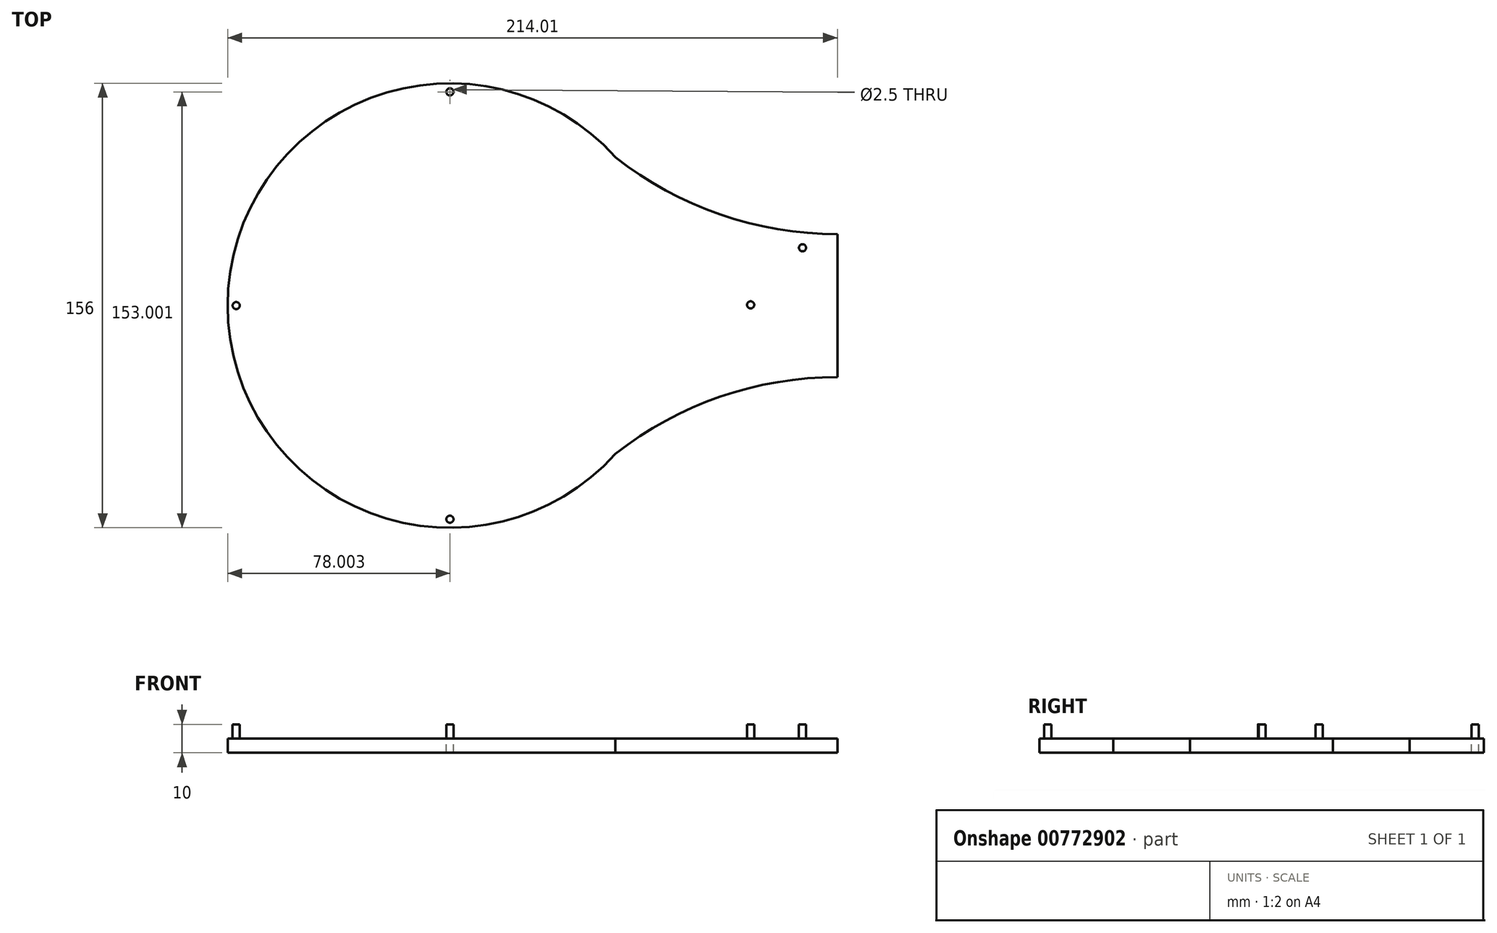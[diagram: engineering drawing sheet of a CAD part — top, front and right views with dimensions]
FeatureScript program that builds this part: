
annotation { "Feature Type Name" : "Feature", "Feature Type Description" : "" }
export const myFeature = defineFeature(function(context is Context, id is Id, definition is map)
    precondition{}
    {
        {
            var Q0;
            Q0=qCreatedBy(makeId("Top.planeOp"),FACE);
            var sketch = newSketch(context, id + "F0", { "sketchPlane" : qUnion([Q0])});
            skArc(sketch, "E0.1", {"start": v(-25.7, 50.9) * mm, "mid": v(-161.83, -1.11) * mm, "end": v(-25.7, -53.14) * mm});
            skLineSegment(sketch, "E0.3", {"start": v(52.19, 17.91) * mm, "end": v(52.17, -20.18) * mm});
            skLineSegment(sketch, "E1", {"start": v(52.18, -1.13) * mm, "end": v(52.18, 23.97) * mm});
            skLineSegment(sketch, "E2", {"start": v(52.18, 23.97) * mm, "end": v(52.18, -26.23) * mm});
            skArc(sketch, "E3", {"start": v(-25.7, 50.9) * mm, "mid": v(10.98, 30.9) * mm, "end": v(52.18, 23.97) * mm});
            skArc(sketch, "E4", {"start": v(52.18, -26.23) * mm, "mid": v(10.97, -33.14) * mm, "end": v(-25.7, -53.14) * mm});
            skPoint(sketch, "E5.startSnap0", {"position": v(-161.83, -1.11) * mm});
            skCircle(sketch, "E6", {"center": v(-83.83, 73.88) * mm, "radius": 1.25 * mm});
            skCircle(sketch, "E7", {"center": v(-158.83, -1.13) * mm, "radius": 1.25 * mm});
            skCircle(sketch, "E8", {"center": v(-83.83, -76.12) * mm, "radius": 1.25 * mm});
            skCircle(sketch, "E9", {"center": v(21.7, -0.89) * mm, "radius": 1.25 * mm});
            skCircle(sketch, "E10", {"center": v(39.93, 19.15) * mm, "radius": 1.25 * mm});
            skSolve(sketch);
        }
        {
            var Q0;
            Q0=makeQuery(id+"F0.imprint","IMPRINT",FACE,{"disambiguationData":[TD([[makeQuery(id+"F0.imprint","IMPRINT",EDGE,{"derivedFrom":sQuery(id+"F0.wireOp",EDGE,"E0.1")}),1.0]])]});
            extrude(context, id + "F1", {"entities" : qUnion([Q0]), "oppositeDirection" : true, "depth" : 5 * mm, "offsetDistance" : 25 * mm});
        }
        {
            var Q0;
            Q0=makeQuery(id+"F0.imprint","IMPRINT",FACE,{"disambiguationData":[TD([[makeQuery(id+"F0.imprint","IMPRINT",EDGE,{"derivedFrom":sQuery(id+"F0.wireOp",EDGE,"E10")}),1.0]])]});
            var Q1;
            Q1=makeQuery(id+"F0.imprint","IMPRINT",FACE,{"disambiguationData":[TD([[makeQuery(id+"F0.imprint","IMPRINT",EDGE,{"derivedFrom":sQuery(id+"F0.wireOp",EDGE,"E9")}),1.0]])]});
            var Q2;
            Q2=makeQuery(id+"F0.imprint","IMPRINT",FACE,{"disambiguationData":[TD([[makeQuery(id+"F0.imprint","IMPRINT",EDGE,{"derivedFrom":sQuery(id+"F0.wireOp",EDGE,"E6")}),1.0]])]});
            var Q3;
            Q3=makeQuery(id+"F0.imprint","IMPRINT",FACE,{"disambiguationData":[TD([[makeQuery(id+"F0.imprint","IMPRINT",EDGE,{"derivedFrom":sQuery(id+"F0.wireOp",EDGE,"E8")}),1.0]])]});
            var Q4;
            Q4=makeQuery(id+"F0.imprint","IMPRINT",FACE,{"disambiguationData":[TD([[makeQuery(id+"F0.imprint","IMPRINT",EDGE,{"derivedFrom":sQuery(id+"F0.wireOp",EDGE,"E7")}),1.0]])]});
            extrude(context, id + "F2", {"entities" : qUnion([Q0, Q1, Q2, Q3, Q4]), "depth" : 5 * mm, "offsetDistance" : 25 * mm});
        }
        {
            var Q0;
            Q0=makeQuery(id+"F0.imprint","IMPRINT",FACE,{"disambiguationData":[TD([[makeQuery(id+"F0.imprint","IMPRINT",EDGE,{"derivedFrom":sQuery(id+"F0.wireOp",EDGE,"E7")}),1.0]])]});
            var Q1;
            Q1=makeQuery(id+"F0.imprint","IMPRINT",FACE,{"disambiguationData":[TD([[makeQuery(id+"F0.imprint","IMPRINT",EDGE,{"derivedFrom":sQuery(id+"F0.wireOp",EDGE,"E8")}),1.0]])]});
            var Q2;
            Q2=makeQuery(id+"F0.imprint","IMPRINT",FACE,{"disambiguationData":[TD([[makeQuery(id+"F0.imprint","IMPRINT",EDGE,{"derivedFrom":sQuery(id+"F0.wireOp",EDGE,"E6")}),1.0]])]});
            var Q3;
            Q3=makeQuery(id+"F0.imprint","IMPRINT",FACE,{"disambiguationData":[TD([[makeQuery(id+"F0.imprint","IMPRINT",EDGE,{"derivedFrom":sQuery(id+"F0.wireOp",EDGE,"E9")}),1.0]])]});
            var Q4;
            Q4=makeQuery(id+"F0.imprint","IMPRINT",FACE,{"disambiguationData":[TD([[makeQuery(id+"F0.imprint","IMPRINT",EDGE,{"derivedFrom":sQuery(id+"F0.wireOp",EDGE,"E10")}),1.0]])]});
            extrude(context, id + "F3", {"entities" : qUnion([Q0, Q1, Q2, Q3, Q4]), "oppositeDirection" : true, "depth" : 5 * mm, "offsetDistance" : 25 * mm});
        }
        {
            var Q0;
            Q0=makeQuery(id+"F1.opExtrude","SWEPT_BODY",BODY,{"disambiguationData":[OSD([sQuery(id+"F0.wireOp",EDGE,"E0.1"),sQuery(id+"F0.wireOp",EDGE,"E2"),sQuery(id+"F0.wireOp",EDGE,"E3"),sQuery(id+"F0.wireOp",EDGE,"E4"),sQuery(id+"F0.wireOp",EDGE,"E6"),sQuery(id+"F0.wireOp",EDGE,"E7"),sQuery(id+"F0.wireOp",EDGE,"E8"),sQuery(id+"F0.wireOp",EDGE,"E9"),sQuery(id+"F0.wireOp",EDGE,"E10")])]});
            var Q1;
            Q1=makeQuery(id+"F2.opExtrude","SWEPT_BODY",BODY,{"disambiguationData":[OSD([sQuery(id+"F0.wireOp",EDGE,"E6")])]});
            var Q2;
            Q2=makeQuery(id+"F2.opExtrude","SWEPT_BODY",BODY,{"disambiguationData":[OSD([sQuery(id+"F0.wireOp",EDGE,"E9")])]});
            var Q3;
            Q3=makeQuery(id+"F3.opExtrude","SWEPT_BODY",BODY,{"disambiguationData":[OSD([sQuery(id+"F0.wireOp",EDGE,"E10")])]});
            var Q4;
            Q4=makeQuery(id+"F3.opExtrude","SWEPT_BODY",BODY,{"disambiguationData":[OSD([sQuery(id+"F0.wireOp",EDGE,"E9")])]});
            var Q5;
            Q5=makeQuery(id+"F3.opExtrude","SWEPT_BODY",BODY,{"disambiguationData":[OSD([sQuery(id+"F0.wireOp",EDGE,"E8")])]});
            var Q6;
            Q6=makeQuery(id+"F3.opExtrude","SWEPT_BODY",BODY,{"disambiguationData":[OSD([sQuery(id+"F0.wireOp",EDGE,"E7")])]});
            booleanBodies(context, id + "F4", {"operationType" : BooleanOperationType.UNION, "tools" : qUnion([Q0, Q1, Q2, Q3, Q4, Q5, Q6])});
        }
    });
